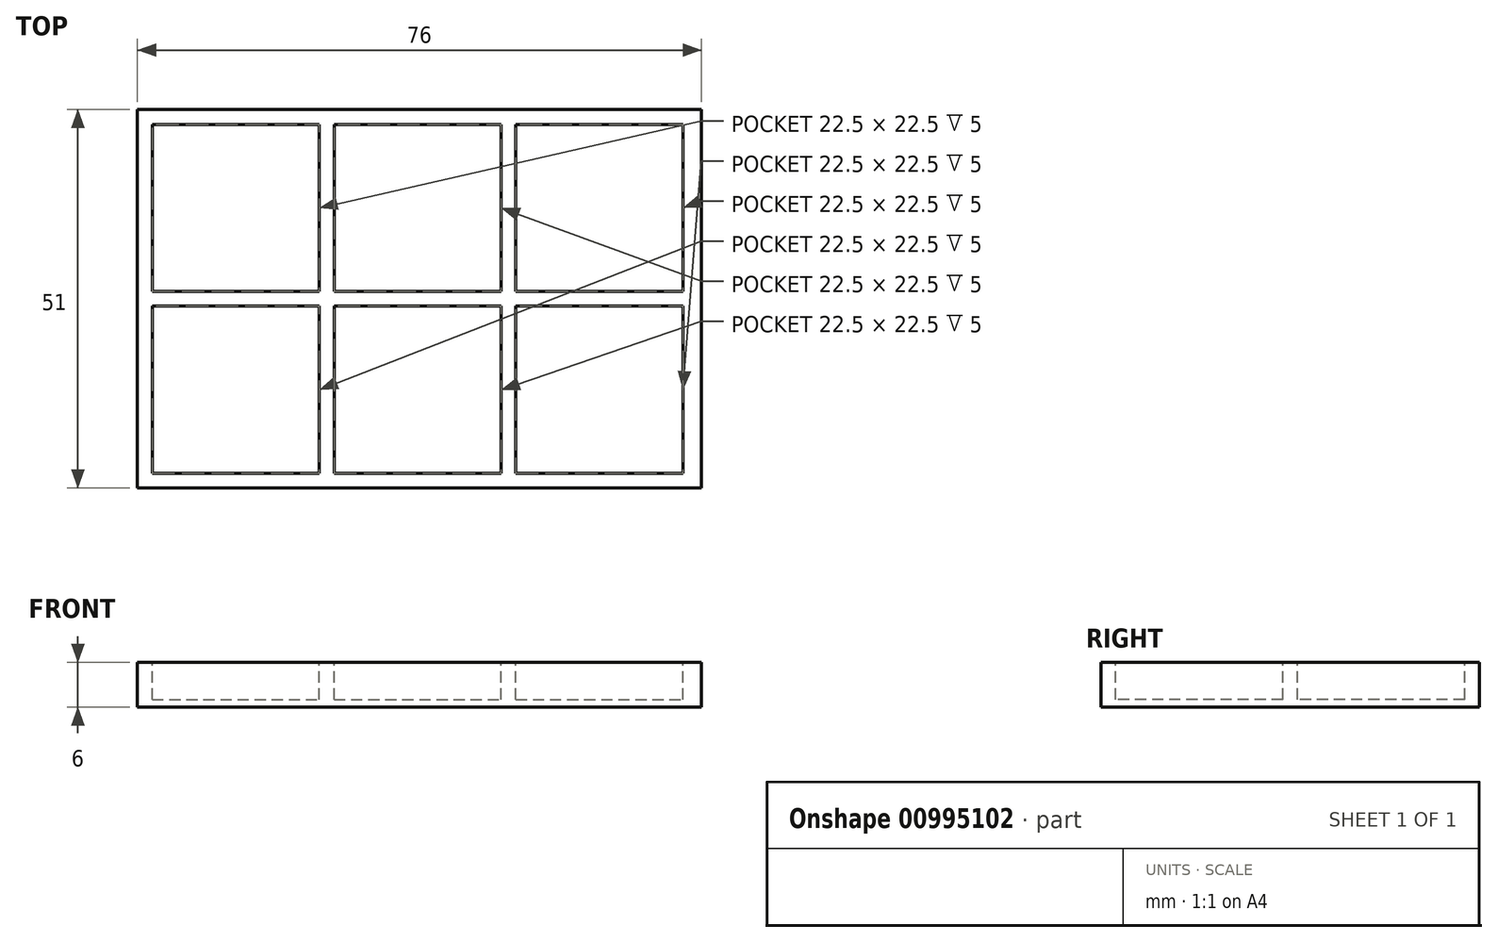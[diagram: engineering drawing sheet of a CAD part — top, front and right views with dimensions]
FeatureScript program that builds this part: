
annotation { "Feature Type Name" : "Feature", "Feature Type Description" : "" }
export const myFeature = defineFeature(function(context is Context, id is Id, definition is map)
    precondition{}
    {
        {
            var Q0;
            Q0=qCreatedBy(makeId("Top.planeOp"),FACE);
            var sketch = newSketch(context, id + "F0", { "sketchPlane" : qUnion([Q0])});
            skLineSegment(sketch, "E0.bottom", {"start": v(38, 25.5) * mm, "end": v(-38, 25.5) * mm});
            skLineSegment(sketch, "E0.top", {"start": v(38, -25.5) * mm, "end": v(-38, -25.5) * mm});
            skLineSegment(sketch, "E0.left", {"start": v(38, 25.5) * mm, "end": v(38, -25.5) * mm});
            skLineSegment(sketch, "E0.right", {"start": v(-38, 25.5) * mm, "end": v(-38, -25.5) * mm});
            skPoint(sketch, "E0.middle", {"position": v(0, 0) * mm});
            skSolve(sketch);
        }
        {
            var Q0;
            Q0 = qSketchRegion(id + "F0", true);
            extrude(context, id + "F1", {"entities" : qUnion([Q0]), "depth" : 6 * mm, "offsetDistance" : 25 * mm});
        }
        {
            var Q0;
            Q0=makeQuery(id+"F1.opExtrude","CAP_FACE",FACE,{"disambiguationData":[OSD([sQuery(id+"F0.wireOp",EDGE,"E0.bottom"),sQuery(id+"F0.wireOp",EDGE,"E0.top"),sQuery(id+"F0.wireOp",EDGE,"E0.left"),sQuery(id+"F0.wireOp",EDGE,"E0.right")])],"isStart":false});
            var sketch = newSketch(context, id + "F2", { "sketchPlane" : qUnion([Q0])});
            skLineSegment(sketch, "E1.bottom", {"start": v(-36, 23.5) * mm, "end": v(-13.5, 23.5) * mm});
            skLineSegment(sketch, "E1.top", {"start": v(-36, 1) * mm, "end": v(-13.5, 1) * mm});
            skLineSegment(sketch, "E1.left", {"start": v(-36, 23.5) * mm, "end": v(-36, 1) * mm});
            skLineSegment(sketch, "E1.right", {"start": v(-13.5, 23.5) * mm, "end": v(-13.5, 1) * mm});
            skLineSegment(sketch, "E2.bottom", {"start": v(13, 23.5) * mm, "end": v(35.5, 23.5) * mm});
            skLineSegment(sketch, "E2.top", {"start": v(13, 1) * mm, "end": v(35.5, 1) * mm});
            skLineSegment(sketch, "E2.left", {"start": v(13, 23.5) * mm, "end": v(13, 1) * mm});
            skLineSegment(sketch, "E2.right", {"start": v(35.5, 23.5) * mm, "end": v(35.5, 1) * mm});
            skLineSegment(sketch, "E3.bottom", {"start": v(-36, -1) * mm, "end": v(-13.5, -1) * mm});
            skLineSegment(sketch, "E3.top", {"start": v(-36, -23.5) * mm, "end": v(-13.5, -23.5) * mm});
            skLineSegment(sketch, "E3.left", {"start": v(-36, -1) * mm, "end": v(-36, -23.5) * mm});
            skLineSegment(sketch, "E3.right", {"start": v(-13.5, -1) * mm, "end": v(-13.5, -23.5) * mm});
            skLineSegment(sketch, "E4.bottom", {"start": v(-11.5, 23.5) * mm, "end": v(11, 23.5) * mm});
            skLineSegment(sketch, "E4.top", {"start": v(-11.5, 1) * mm, "end": v(11, 1) * mm});
            skLineSegment(sketch, "E4.left", {"start": v(-11.5, 23.5) * mm, "end": v(-11.5, 1) * mm});
            skLineSegment(sketch, "E4.right", {"start": v(11, 23.5) * mm, "end": v(11, 1) * mm});
            skLineSegment(sketch, "E5.bottom", {"start": v(-11.5, -1) * mm, "end": v(11, -1) * mm});
            skLineSegment(sketch, "E5.top", {"start": v(-11.5, -23.5) * mm, "end": v(11, -23.5) * mm});
            skLineSegment(sketch, "E5.left", {"start": v(-11.5, -1) * mm, "end": v(-11.5, -23.5) * mm});
            skLineSegment(sketch, "E5.right", {"start": v(11, -1) * mm, "end": v(11, -23.5) * mm});
            skLineSegment(sketch, "E6.bottom", {"start": v(13, -1) * mm, "end": v(35.5, -1) * mm});
            skLineSegment(sketch, "E6.top", {"start": v(13, -23.5) * mm, "end": v(35.5, -23.5) * mm});
            skLineSegment(sketch, "E6.left", {"start": v(13, -1) * mm, "end": v(13, -23.5) * mm});
            skLineSegment(sketch, "E6.right", {"start": v(35.5, -1) * mm, "end": v(35.5, -23.5) * mm});
            skSolve(sketch);
        }
        {
            var Q0;
            Q0 = qSketchRegion(id + "F2", true);
            extrude(context, id + "F3", {"entities" : qUnion([Q0]), "operationType" : NewBodyOperationType.REMOVE, "oppositeDirection" : true, "depth" : 5 * mm, "offsetDistance" : 25 * mm});
        }
    });
